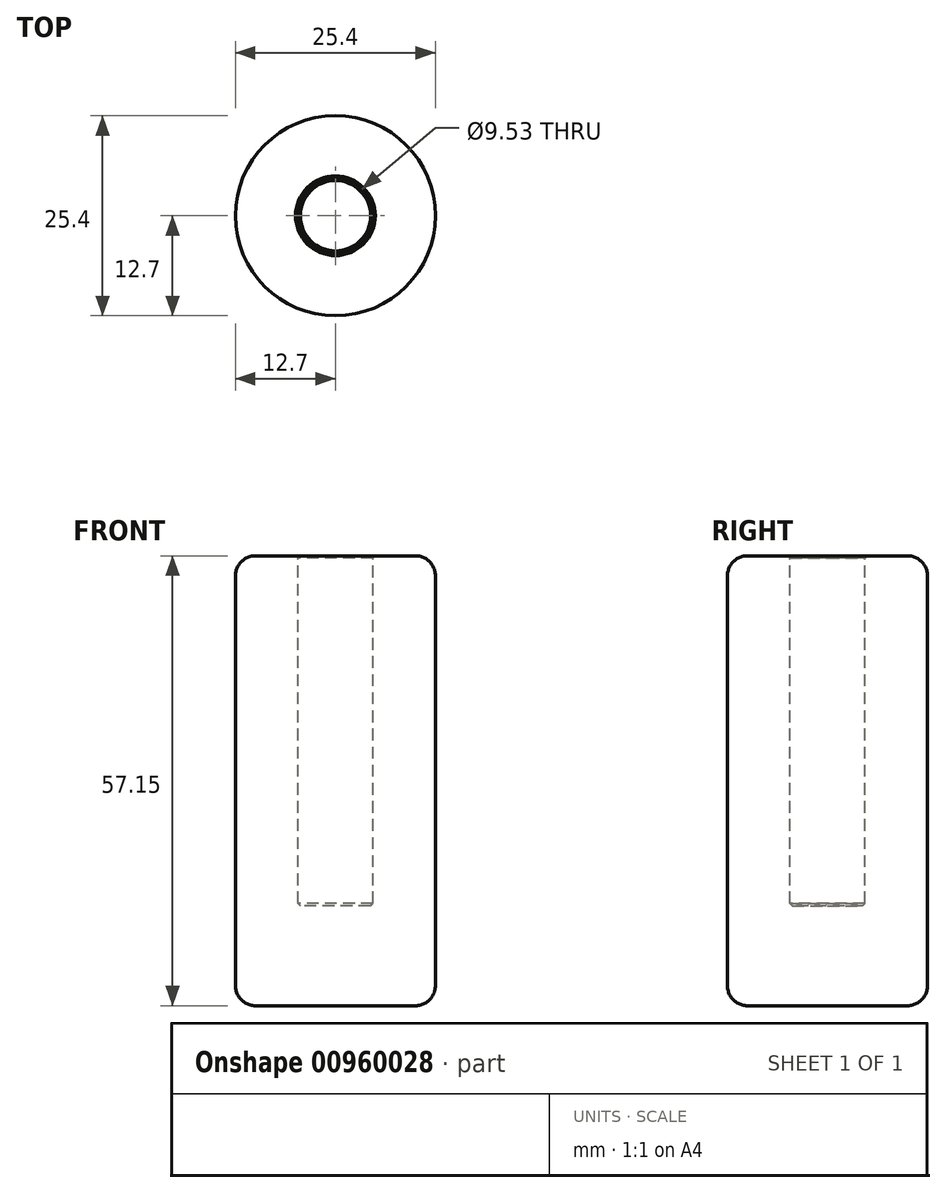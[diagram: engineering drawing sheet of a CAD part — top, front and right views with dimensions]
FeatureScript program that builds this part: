
annotation { "Feature Type Name" : "Feature", "Feature Type Description" : "" }
export const myFeature = defineFeature(function(context is Context, id is Id, definition is map)
    precondition{}
    {
        {
            var Q0;
            Q0=qCreatedBy(makeId("Top.planeOp"),FACE);
            var sketch = newSketch(context, id + "F0", { "sketchPlane" : qUnion([Q0])});
            skCircle(sketch, "E0", {"center": v(0, 0) * mm, "radius": 12.7 * mm});
            skSolve(sketch);
        }
        {
            var Q0;
            Q0=qSketchRegion(id+"F0",true);
            extrude(context, id + "F1", {"entities" : qUnion([Q0]), "depth" : 57.15 * mm, "offsetDistance" : 25.4 * mm});
        }
        {
            var Q0;
            Q0=makeQuery(id+"F1.opExtrude","CAP_FACE",FACE,{"disambiguationData":[OSD([sQuery(id+"F0.wireOp",EDGE,"E0")])],"isStart":false});
            var sketch = newSketch(context, id + "F2", { "sketchPlane" : qUnion([Q0])});
            skCircle(sketch, "E1", {"center": v(0, 0) * mm, "radius": 4.76 * mm});
            skSolve(sketch);
        }
        {
            var Q0;
            Q0=qSketchRegion(id+"F2",true);
            extrude(context, id + "F3", {"entities" : qUnion([Q0]), "operationType" : NewBodyOperationType.REMOVE, "oppositeDirection" : true, "depth" : 44.45 * mm, "offsetDistance" : 25.4 * mm});
        }
        {
            var Q0;
            Q0=makeQuery(id+"F1.opExtrude","CAP_FACE",FACE,{"disambiguationData":[OSD([sQuery(id+"F0.wireOp",EDGE,"E0")])],"isStart":true});
            var Q1;
            Q1=makeQuery(id+"F1.opExtrude","CAP_EDGE",EDGE,{"disambiguationData":[OSD([sQuery(id+"F0.wireOp",EDGE,"E0")])],"isStart":false});
            fillet(context, id + "F4", {"entities" : qUnion([Q0, Q1]), "radius" : 2.54 * mm, "tangentPropagation" : true, "allowEdgeOverflow" : false});
        }
        {
            var Q0;
            Q0=makeQuery(id+"F3.boolean.opBoolean","COPY",EDGE,{"derivedFrom":makeQuery(id+"F3.opExtrude","CAP_EDGE",EDGE,{"disambiguationData":[OSD([sQuery(id+"F2.wireOp",EDGE,"E1")])],"isStart":false})});
            var Q1;
            Q1=makeQuery(id+"F1.opExtrude","CAP_FACE",FACE,{"disambiguationData":[OSD([sQuery(id+"F0.wireOp",EDGE,"E0")])],"isStart":false});
            chamfer(context, id + "F5", {"entities" : qUnion([Q0, Q1]), "width" : .3 * mm, "tangentPropagation" : true});
        }
    });
